# Revit family: Mixer_Basin_Nero_Classic_PushButton
name_source: partatom
category: Plumbing Fixtures
units: mm (PartAtom-declared; Revit-internal decimal feet)

## family parameters
Always vertical = Yes
Cut with Voids When Loaded = Yes
Maintain Annotation Orientation = No
OmniClass Number = 23.31.00.00
Part Type = Normal
Room Calculation Point = No
Round Connector Dimension = Use Diameter
Shared = No
Work Plane-Based = No

## types (1)
- Chrome (NR291201CH)
    Assembly Code = D2010
    BodyMaterial = Metal_Chrome_Nero
    CW Connection = No
    CWFU = 0
    Cost = 0 $
    Default Elevation = 0 mm  [stored 0 ft]
    Description = Classic Push Tap Chrome
    HW Connection = No
    HWFU = 0
    IfcExportAs = IfcSanitaryTerminal
    IfcExportType = NOTDEFINED
    Manufacturer = Nero
    ManufacturerOverallDepth = 145.5 mm  [stored 0.477362 ft]
    ManufacturerOverallHeight = 82 mm
    ManufacturerOverallWidth = 47.5 mm  [stored 0.15584 ft]
    ManufacturerSpecCode = NR291201CH
    ManufacturerURLProductSpecific = https://nerotapware.com.au
    Model = NR291201CH
    ModifiedIssue = 20241210 $
    Type Comments = Mixer - Basin - Push Button - Chrome
    URL = https://nerotapware.com.au
    Uniclass2015Code = Pr_40_20_87
    Uniclass2015Title = Taps and water supply outlet fittings
    Uniclass2015Version = Products v1.35
    Vent Connection = No
    WFU = 0
    Waste Connection = No

note: [stored X ft] marks values corroborated as IEEE doubles in the binary element streams (Revit-internal decimal feet)

## geometry (parser evidence)
native form markers: Sweep x1
no freeform markers — native parametric forms only
